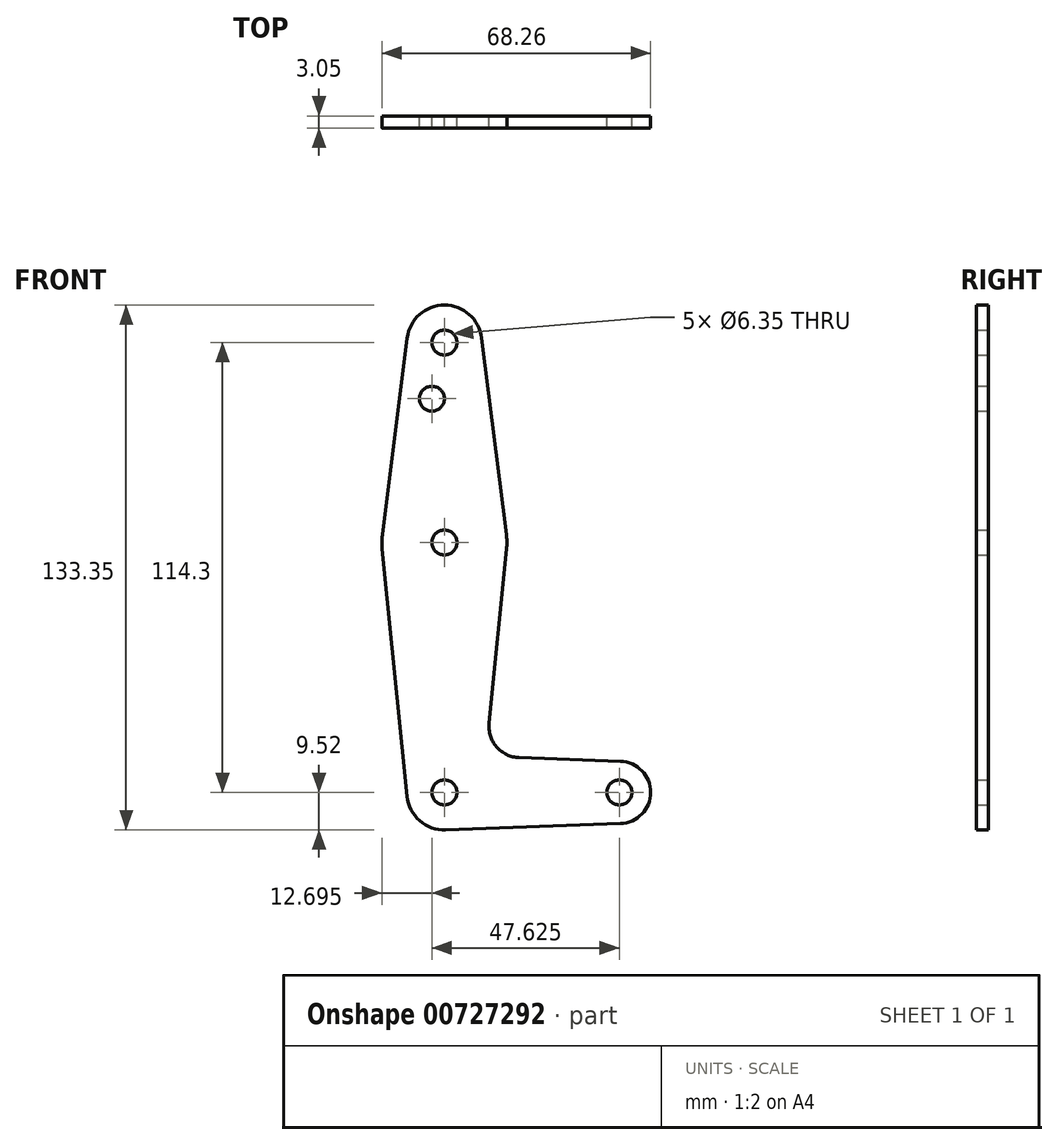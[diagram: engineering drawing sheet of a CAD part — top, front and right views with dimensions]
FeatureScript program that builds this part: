
annotation { "Feature Type Name" : "Feature", "Feature Type Description" : "" }
export const myFeature = defineFeature(function(context is Context, id is Id, definition is map)
    precondition{}
    {
        {
            var Q0;
            Q0=qCreatedBy(makeId("Front.planeOp"),FACE);
            var sketch = newSketch(context, id + "F0", { "sketchPlane" : qUnion([Q0])});
            skLineSegment(sketch, "E0", {"start": v(0, 0) * mm, "end": v(0, 114.3) * mm, "construction": true});
            skLineSegment(sketch, "E1", {"start": v(0, 0) * mm, "end": v(44.45, 0) * mm, "construction": true});
            skCircle(sketch, "E2", {"center": v(0, 0) * mm, "radius": 9.53 * mm});
            skCircle(sketch, "E3", {"center": v(44.45, 0) * mm, "radius": 7.94 * mm});
            skCircle(sketch, "E4", {"center": v(0, 114.3) * mm, "radius": 9.53 * mm});
            skCircle(sketch, "E5", {"center": v(0, 63.5) * mm, "radius": 15.88 * mm});
            skLineSegment(sketch, "E6", {"start": v(9.45, 115.5) * mm, "end": v(15.75, 65.48) * mm});
            skLineSegment(sketch, "E7", {"start": v(-9.45, 115.5) * mm, "end": v(-15.75, 65.48) * mm});
            skLineSegment(sketch, "E8", {"start": v(-15.8, 61.91) * mm, "end": v(-9.48, -0.95) * mm});
            skLineSegment(sketch, "E9", {"start": v(15.8, 61.91) * mm, "end": v(11.34, 17.6) * mm});
            skLineSegment(sketch, "E10", {"start": v(18.97, 8.85) * mm, "end": v(44.73, 7.93) * mm});
            skLineSegment(sketch, "E11", {"start": v(0.34, -9.52) * mm, "end": v(44.73, -7.93) * mm});
            skCircle(sketch, "E12", {"center": v(0, 114.3) * mm, "radius": 3.18 * mm});
            skCircle(sketch, "E13", {"center": v(0, 63.5) * mm, "radius": 3.18 * mm});
            skCircle(sketch, "E14", {"center": v(0, 0) * mm, "radius": 3.18 * mm});
            skCircle(sketch, "E15", {"center": v(44.45, 0) * mm, "radius": 3.18 * mm});
            skArc(sketch, "E16.filletArc", {"start": v(11.34, 17.6) * mm, "mid": v(13.26, 11.57) * mm, "end": v(18.97, 8.85) * mm});
            skCircle(sketch, "E17", {"center": v(-3.18, 100.03) * mm, "radius": 3.18 * mm});
            skSolve(sketch);
        }
        {
            var Q0;
            Q0 = qSketchRegion(id + "F0", true);
            extrude(context, id + "F1", {"entities" : qUnion([Q0]), "depth" : 3.05 * mm, "offsetDistance" : 25.4 * mm});
        }
    });
